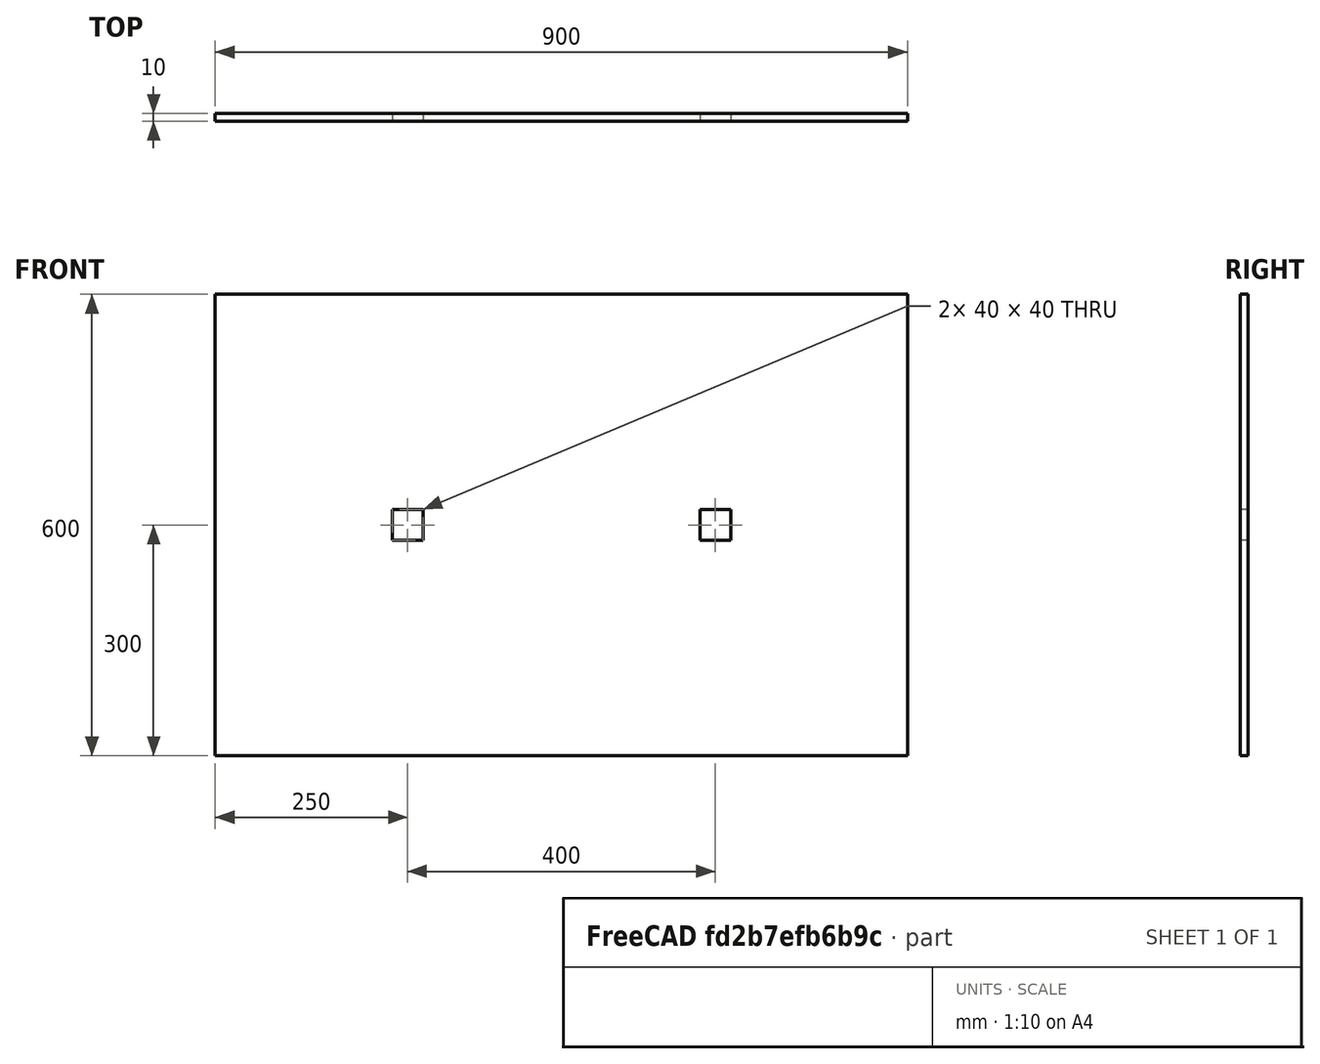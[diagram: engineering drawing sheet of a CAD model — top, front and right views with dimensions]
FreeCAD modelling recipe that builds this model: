
FCSTD DOCUMENT  (FreeCAD 1.0R39319 (Git))
Label: Chapa_Inf
License: All rights reserved
LicenseURL: https://en.wikipedia.org/wiki/All_rights_reserved
objects: Sketcher::SketchObject×1, PartDesign::Pad×1, PartDesign::Body×1
note: 6 computed .brp shape members not serialized (recipe doc carries the construction recipe); baked Part::Feature solids carry a one-line shape summary decoded from their .brp

FEATURE [Sketcher::SketchObject] Sketch
  ArcFitTolerance = 1e-06
  AttachmentSupport = -> [XZ_Plane]
  FullyConstrained = false
  MakeInternals = false
  MapMode = 5
  Placement = pos=(0,0,0) rot=(1,0,0;1.5708rad)
  sketch-geometry (15):
    g0: LineSegment StartX=-450 StartY=-300 StartZ=0 EndX=450 EndY=-300 EndZ=0
    g1: LineSegment StartX=450 StartY=-300 StartZ=0 EndX=450 EndY=300 EndZ=0
    g2: LineSegment StartX=450 StartY=300 StartZ=0 EndX=-450 EndY=300 EndZ=0
    g3: LineSegment StartX=-450 StartY=300 StartZ=0 EndX=-450 EndY=-300 EndZ=0
    g4: GeomPoint [constr] X=0 Y=0 Z=0
    g5: LineSegment StartX=-220 StartY=-20 StartZ=0 EndX=-180 EndY=-20 EndZ=0
    g6: LineSegment StartX=-180 StartY=-20 StartZ=0 EndX=-180 EndY=20 EndZ=0
    g7: LineSegment StartX=-180 StartY=20 StartZ=0 EndX=-220 EndY=20 EndZ=0
    g8: LineSegment StartX=-220 StartY=20 StartZ=0 EndX=-220 EndY=-20 EndZ=0
    g9: GeomPoint [constr] X=-200 Y=0 Z=0
    g10: LineSegment StartX=220 StartY=-20 StartZ=0 EndX=180 EndY=-20 EndZ=0
    g11: LineSegment StartX=180 StartY=-20 StartZ=0 EndX=180 EndY=20 EndZ=0
    g12: LineSegment StartX=180 StartY=20 StartZ=0 EndX=220 EndY=20 EndZ=0
    g13: LineSegment StartX=220 StartY=20 StartZ=0 EndX=220 EndY=-20 EndZ=0
    g14: GeomPoint [constr] X=200 Y=0 Z=0
  constraints (34):
    c: Coincident(g0,g1)
    c: Coincident(g1,g2)
    c: Coincident(g2,g3)
    c: Coincident(g3,g0)
    c: Horizontal(g0)
    c: Horizontal(g2)
    c: Vertical(g1)
    c: Vertical(g3)
    c: Symmetric(g2,g0,g4)
    c: Distance(g1,g3) = 900
    c: Distance(g0,g2) = 600
    c: Coincident(g4,g-1)
    c: Coincident(g5,g6)
    c: Coincident(g6,g7)
    c: Coincident(g7,g8)
    c: Coincident(g8,g5)
    c: Horizontal(g5)
    c: Horizontal(g7)
    c: Vertical(g6)
    c: Vertical(g8)
    c: Symmetric(g7,g5,g9)
    c: PointOnObject(g9,g-1)
    c: DistanceY(g6,g6) = 40
    c: DistanceX(g7,g7) = 40
    c: DistanceX(g9,g-1) = 200
    c: Coincident(g10,g11)
    c: Coincident(g11,g12)
    c: Coincident(g12,g13)
    c: Coincident(g13,g10)
    c: Horizontal(g10)
    c: Horizontal(g12)
    c: Vertical(g11)
    c: Vertical(g13)
    c: Symmetric(g12,g10,g14)
FEATURE [PartDesign::Pad] Pad
  Direction = (0,-1,2e-16)
  Length = 10
  Length2 = 10
  Placement = pos=(0,0,0) rot=(1,0,0;1.5708rad)
  Profile = -> Sketch
  ReferenceAxis = -> Sketch [N_Axis]
  Refine = true
  Suppressed = false
  Type = 0
FEATURE [PartDesign::Body] Body
  AllowCompound = false
  Group = -> [Sketch,Pad]
  Origin = -> Origin
  Tip = -> Pad
